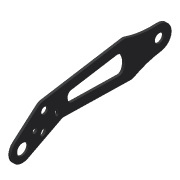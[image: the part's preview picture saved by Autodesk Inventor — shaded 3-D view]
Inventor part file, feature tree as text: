
AUTODESK INVENTOR PART (.ipt)
format: ipt  version: 2019.4 (Build 234330000, 330)  size: 185,344 bytes
history: native  units: mm
features: hole x3, other x1, sketch x1, extrude x1
ambient origin geometry x8: Origin, YZ Plane, XZ Plane, XY Plane, X Axis, Y Axis, Z Axis, Center Point
bodies: Body1 (feature_tree)
feature tree (6):
  other  "ソリッド1"
  sketch  "スケッチ1"
  extrude  "押し出し1"  Depth=125.0mm
  hole  "穴1"  [1 undecoded]
  hole  "穴2"  [1 undecoded]
  hole  "穴3"  [1 undecoded]
note: 3 required parameter values undecoded (feature->parameter linkage not recoverable at this tier; creation-order binding heuristic only, values carry confidence <= 0.55)
